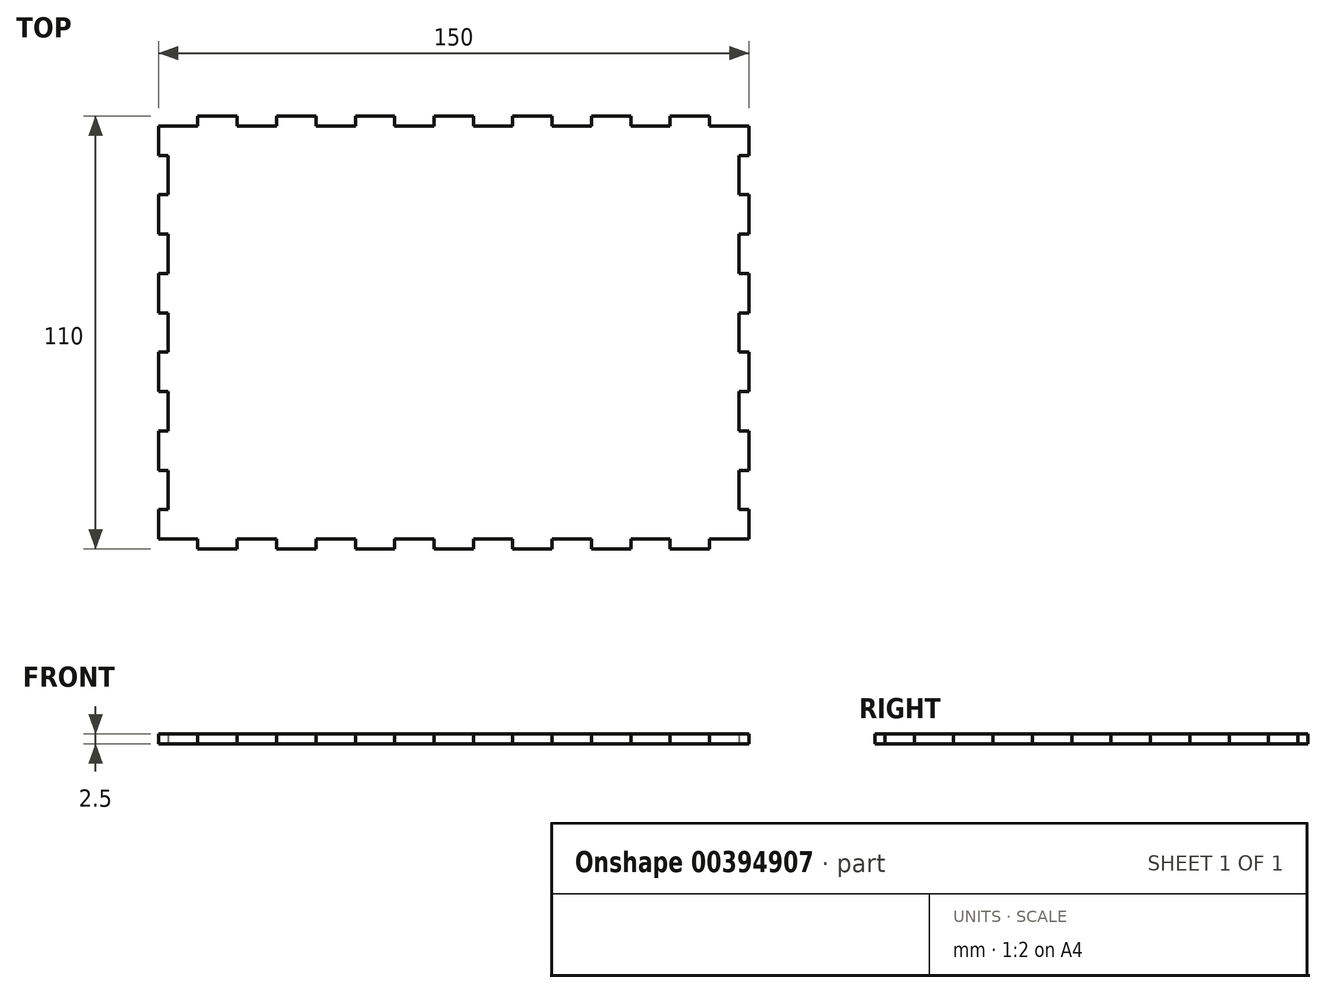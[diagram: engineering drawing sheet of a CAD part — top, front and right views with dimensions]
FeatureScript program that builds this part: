
annotation { "Feature Type Name" : "Feature", "Feature Type Description" : "" }
export const myFeature = defineFeature(function(context is Context, id is Id, definition is map)
    precondition{}
    {
        {
            var Q0;
            Q0=qCreatedBy(makeId("Top.planeOp"),FACE);
            var sketch = newSketch(context, id + "F0", { "sketchPlane" : qUnion([Q0])});
            skLineSegment(sketch, "E0.bottom", {"start": v(75, -55) * mm, "end": v(-75, -55) * mm});
            skLineSegment(sketch, "E0.top", {"start": v(75, 55) * mm, "end": v(-75, 55) * mm});
            skLineSegment(sketch, "E0.left", {"start": v(75, -55) * mm, "end": v(75, 55) * mm});
            skLineSegment(sketch, "E0.right", {"start": v(-75, -55) * mm, "end": v(-75, 55) * mm});
            skLineSegment(sketch, "E1.bottom", {"start": v(75, 55) * mm, "end": v(65, 55) * mm});
            skLineSegment(sketch, "E1.top", {"start": v(75, 52.5) * mm, "end": v(65, 52.5) * mm});
            skLineSegment(sketch, "E1.left", {"start": v(75, 55) * mm, "end": v(75, 52.5) * mm});
            skLineSegment(sketch, "E1.right", {"start": v(65, 55) * mm, "end": v(65, 52.5) * mm});
            skLineSegment(sketch, "E2.0.1.0", {"start": v(65, -52.5) * mm, "end": v(65, -55) * mm});
            skLineSegment(sketch, "E2.0.1.1", {"start": v(75, -52.5) * mm, "end": v(75, -55) * mm});
            skLineSegment(sketch, "E2.0.1.2", {"start": v(75, -55) * mm, "end": v(65, -55) * mm});
            skLineSegment(sketch, "E2.0.1.3", {"start": v(75, -52.5) * mm, "end": v(65, -52.5) * mm});
            skLineSegment(sketch, "E2.1.0.0", {"start": v(45, 55) * mm, "end": v(45, 52.5) * mm});
            skLineSegment(sketch, "E2.1.0.1", {"start": v(55, 55) * mm, "end": v(55, 52.5) * mm});
            skLineSegment(sketch, "E2.1.0.2", {"start": v(55, 52.5) * mm, "end": v(45, 52.5) * mm});
            skLineSegment(sketch, "E2.1.0.3", {"start": v(55, 55) * mm, "end": v(45, 55) * mm});
            skLineSegment(sketch, "E2.1.1.0", {"start": v(45, -52.5) * mm, "end": v(45, -55) * mm});
            skLineSegment(sketch, "E2.1.1.1", {"start": v(55, -52.5) * mm, "end": v(55, -55) * mm});
            skLineSegment(sketch, "E2.1.1.2", {"start": v(55, -55) * mm, "end": v(45, -55) * mm});
            skLineSegment(sketch, "E2.1.1.3", {"start": v(55, -52.5) * mm, "end": v(45, -52.5) * mm});
            skLineSegment(sketch, "E2.2.0.0", {"start": v(25, 55) * mm, "end": v(25, 52.5) * mm});
            skLineSegment(sketch, "E2.2.0.1", {"start": v(35, 55) * mm, "end": v(35, 52.5) * mm});
            skLineSegment(sketch, "E2.2.0.2", {"start": v(35, 52.5) * mm, "end": v(25, 52.5) * mm});
            skLineSegment(sketch, "E2.2.0.3", {"start": v(35, 55) * mm, "end": v(25, 55) * mm});
            skLineSegment(sketch, "E2.2.1.0", {"start": v(25, -52.5) * mm, "end": v(25, -55) * mm});
            skLineSegment(sketch, "E2.2.1.1", {"start": v(35, -52.5) * mm, "end": v(35, -55) * mm});
            skLineSegment(sketch, "E2.2.1.2", {"start": v(35, -55) * mm, "end": v(25, -55) * mm});
            skLineSegment(sketch, "E2.2.1.3", {"start": v(35, -52.5) * mm, "end": v(25, -52.5) * mm});
            skLineSegment(sketch, "E2.3.0.0", {"start": v(5, 55) * mm, "end": v(5, 52.5) * mm});
            skLineSegment(sketch, "E2.3.0.1", {"start": v(15, 55) * mm, "end": v(15, 52.5) * mm});
            skLineSegment(sketch, "E2.3.0.2", {"start": v(15, 52.5) * mm, "end": v(5, 52.5) * mm});
            skLineSegment(sketch, "E2.3.0.3", {"start": v(15, 55) * mm, "end": v(5, 55) * mm});
            skLineSegment(sketch, "E2.3.1.0", {"start": v(5, -52.5) * mm, "end": v(5, -55) * mm});
            skLineSegment(sketch, "E2.3.1.1", {"start": v(15, -52.5) * mm, "end": v(15, -55) * mm});
            skLineSegment(sketch, "E2.3.1.2", {"start": v(15, -55) * mm, "end": v(5, -55) * mm});
            skLineSegment(sketch, "E2.3.1.3", {"start": v(15, -52.5) * mm, "end": v(5, -52.5) * mm});
            skLineSegment(sketch, "E2.4.0.0", {"start": v(-15, 55) * mm, "end": v(-15, 52.5) * mm});
            skLineSegment(sketch, "E2.4.0.1", {"start": v(-5, 55) * mm, "end": v(-5, 52.5) * mm});
            skLineSegment(sketch, "E2.4.0.2", {"start": v(-5, 52.5) * mm, "end": v(-15, 52.5) * mm});
            skLineSegment(sketch, "E2.4.0.3", {"start": v(-5, 55) * mm, "end": v(-15, 55) * mm});
            skLineSegment(sketch, "E2.4.1.0", {"start": v(-15, -52.5) * mm, "end": v(-15, -55) * mm});
            skLineSegment(sketch, "E2.4.1.1", {"start": v(-5, -52.5) * mm, "end": v(-5, -55) * mm});
            skLineSegment(sketch, "E2.4.1.2", {"start": v(-5, -55) * mm, "end": v(-15, -55) * mm});
            skLineSegment(sketch, "E2.4.1.3", {"start": v(-5, -52.5) * mm, "end": v(-15, -52.5) * mm});
            skLineSegment(sketch, "E2.5.0.0", {"start": v(-35, 55) * mm, "end": v(-35, 52.5) * mm});
            skLineSegment(sketch, "E2.5.0.1", {"start": v(-25, 55) * mm, "end": v(-25, 52.5) * mm});
            skLineSegment(sketch, "E2.5.0.2", {"start": v(-25, 52.5) * mm, "end": v(-35, 52.5) * mm});
            skLineSegment(sketch, "E2.5.0.3", {"start": v(-25, 55) * mm, "end": v(-35, 55) * mm});
            skLineSegment(sketch, "E2.5.1.0", {"start": v(-35, -52.5) * mm, "end": v(-35, -55) * mm});
            skLineSegment(sketch, "E2.5.1.1", {"start": v(-25, -52.5) * mm, "end": v(-25, -55) * mm});
            skLineSegment(sketch, "E2.5.1.2", {"start": v(-25, -55) * mm, "end": v(-35, -55) * mm});
            skLineSegment(sketch, "E2.5.1.3", {"start": v(-25, -52.5) * mm, "end": v(-35, -52.5) * mm});
            skLineSegment(sketch, "E2.6.0.0", {"start": v(-55, 55) * mm, "end": v(-55, 52.5) * mm});
            skLineSegment(sketch, "E2.6.0.1", {"start": v(-45, 55) * mm, "end": v(-45, 52.5) * mm});
            skLineSegment(sketch, "E2.6.0.2", {"start": v(-45, 52.5) * mm, "end": v(-55, 52.5) * mm});
            skLineSegment(sketch, "E2.6.0.3", {"start": v(-45, 55) * mm, "end": v(-55, 55) * mm});
            skLineSegment(sketch, "E2.6.1.0", {"start": v(-55, -52.5) * mm, "end": v(-55, -55) * mm});
            skLineSegment(sketch, "E2.6.1.1", {"start": v(-45, -52.5) * mm, "end": v(-45, -55) * mm});
            skLineSegment(sketch, "E2.6.1.2", {"start": v(-45, -55) * mm, "end": v(-55, -55) * mm});
            skLineSegment(sketch, "E2.6.1.3", {"start": v(-45, -52.5) * mm, "end": v(-55, -52.5) * mm});
            skLineSegment(sketch, "E2.7.0.0", {"start": v(-75, 55) * mm, "end": v(-75, 52.5) * mm});
            skLineSegment(sketch, "E2.7.0.1", {"start": v(-65, 55) * mm, "end": v(-65, 52.5) * mm});
            skLineSegment(sketch, "E2.7.0.2", {"start": v(-65, 52.5) * mm, "end": v(-75, 52.5) * mm});
            skLineSegment(sketch, "E2.7.0.3", {"start": v(-65, 55) * mm, "end": v(-75, 55) * mm});
            skLineSegment(sketch, "E2.7.1.0", {"start": v(-75, -52.5) * mm, "end": v(-75, -55) * mm});
            skLineSegment(sketch, "E2.7.1.1", {"start": v(-65, -52.5) * mm, "end": v(-65, -55) * mm});
            skLineSegment(sketch, "E2.7.1.2", {"start": v(-65, -55) * mm, "end": v(-75, -55) * mm});
            skLineSegment(sketch, "E2.7.1.3", {"start": v(-65, -52.5) * mm, "end": v(-75, -52.5) * mm});
            skLineSegment(sketch, "E2.direction1", {"start": v(65, 52.5) * mm, "end": v(45, 52.5) * mm, "construction": true});
            skLineSegment(sketch, "E2.direction2", {"start": v(65, 52.5) * mm, "end": v(65, -55) * mm, "construction": true});
            skLineSegment(sketch, "E3", {"start": v(-75, 52.5) * mm, "end": v(-75, 45) * mm, "construction": true});
            skLineSegment(sketch, "E4.bottom", {"start": v(-75, 45) * mm, "end": v(-72.5, 45) * mm});
            skLineSegment(sketch, "E4.top", {"start": v(-75, 35) * mm, "end": v(-72.5, 35) * mm});
            skLineSegment(sketch, "E4.left", {"start": v(-75, 45) * mm, "end": v(-75, 35) * mm});
            skLineSegment(sketch, "E4.right", {"start": v(-72.5, 45) * mm, "end": v(-72.5, 35) * mm});
            skLineSegment(sketch, "E5.0.1.0", {"start": v(-72.5, 25) * mm, "end": v(-72.5, 15) * mm});
            skLineSegment(sketch, "E5.0.1.1", {"start": v(-75, 25) * mm, "end": v(-75, 15) * mm});
            skLineSegment(sketch, "E5.0.1.2", {"start": v(-75, 25) * mm, "end": v(-72.5, 25) * mm});
            skLineSegment(sketch, "E5.0.1.3", {"start": v(-75, 15) * mm, "end": v(-72.5, 15) * mm});
            skLineSegment(sketch, "E5.0.2.0", {"start": v(-72.5, 5) * mm, "end": v(-72.5, -5) * mm});
            skLineSegment(sketch, "E5.0.2.1", {"start": v(-75, 5) * mm, "end": v(-75, -5) * mm});
            skLineSegment(sketch, "E5.0.2.2", {"start": v(-75, 5) * mm, "end": v(-72.5, 5) * mm});
            skLineSegment(sketch, "E5.0.2.3", {"start": v(-75, -5) * mm, "end": v(-72.5, -5) * mm});
            skLineSegment(sketch, "E5.0.3.0", {"start": v(-72.5, -15) * mm, "end": v(-72.5, -25) * mm});
            skLineSegment(sketch, "E5.0.3.1", {"start": v(-75, -15) * mm, "end": v(-75, -25) * mm});
            skLineSegment(sketch, "E5.0.3.2", {"start": v(-75, -15) * mm, "end": v(-72.5, -15) * mm});
            skLineSegment(sketch, "E5.0.3.3", {"start": v(-75, -25) * mm, "end": v(-72.5, -25) * mm});
            skLineSegment(sketch, "E5.0.4.0", {"start": v(-72.5, -35) * mm, "end": v(-72.5, -45) * mm});
            skLineSegment(sketch, "E5.0.4.1", {"start": v(-75, -35) * mm, "end": v(-75, -45) * mm});
            skLineSegment(sketch, "E5.0.4.2", {"start": v(-75, -35) * mm, "end": v(-72.5, -35) * mm});
            skLineSegment(sketch, "E5.0.4.3", {"start": v(-75, -45) * mm, "end": v(-72.5, -45) * mm});
            skLineSegment(sketch, "E5.1.0.0", {"start": v(75, 45) * mm, "end": v(75, 35) * mm});
            skLineSegment(sketch, "E5.1.0.1", {"start": v(72.5, 45) * mm, "end": v(72.5, 35) * mm});
            skLineSegment(sketch, "E5.1.0.2", {"start": v(72.5, 45) * mm, "end": v(75, 45) * mm});
            skLineSegment(sketch, "E5.1.0.3", {"start": v(72.5, 35) * mm, "end": v(75, 35) * mm});
            skLineSegment(sketch, "E5.1.1.0", {"start": v(75, 25) * mm, "end": v(75, 15) * mm});
            skLineSegment(sketch, "E5.1.1.1", {"start": v(72.5, 25) * mm, "end": v(72.5, 15) * mm});
            skLineSegment(sketch, "E5.1.1.2", {"start": v(72.5, 25) * mm, "end": v(75, 25) * mm});
            skLineSegment(sketch, "E5.1.1.3", {"start": v(72.5, 15) * mm, "end": v(75, 15) * mm});
            skLineSegment(sketch, "E5.1.2.0", {"start": v(75, 5) * mm, "end": v(75, -5) * mm});
            skLineSegment(sketch, "E5.1.2.1", {"start": v(72.5, 5) * mm, "end": v(72.5, -5) * mm});
            skLineSegment(sketch, "E5.1.2.2", {"start": v(72.5, 5) * mm, "end": v(75, 5) * mm});
            skLineSegment(sketch, "E5.1.2.3", {"start": v(72.5, -5) * mm, "end": v(75, -5) * mm});
            skLineSegment(sketch, "E5.1.3.0", {"start": v(75, -15) * mm, "end": v(75, -25) * mm});
            skLineSegment(sketch, "E5.1.3.1", {"start": v(72.5, -15) * mm, "end": v(72.5, -25) * mm});
            skLineSegment(sketch, "E5.1.3.2", {"start": v(72.5, -15) * mm, "end": v(75, -15) * mm});
            skLineSegment(sketch, "E5.1.3.3", {"start": v(72.5, -25) * mm, "end": v(75, -25) * mm});
            skLineSegment(sketch, "E5.1.4.0", {"start": v(75, -35) * mm, "end": v(75, -45) * mm});
            skLineSegment(sketch, "E5.1.4.1", {"start": v(72.5, -35) * mm, "end": v(72.5, -45) * mm});
            skLineSegment(sketch, "E5.1.4.2", {"start": v(72.5, -35) * mm, "end": v(75, -35) * mm});
            skLineSegment(sketch, "E5.1.4.3", {"start": v(72.5, -45) * mm, "end": v(75, -45) * mm});
            skLineSegment(sketch, "E5.direction1", {"start": v(-72.5, 35) * mm, "end": v(75, 35) * mm, "construction": true});
            skLineSegment(sketch, "E5.direction2", {"start": v(-72.5, 35) * mm, "end": v(-72.5, 15) * mm, "construction": true});
            skSolve(sketch);
        }
        {
            var Q0;
            Q0=makeQuery(id+"F0.imprint","IMPRINT",FACE,{"disambiguationData":[TD([[makeQuery(id+"F0.imprint","IMPRINT",EDGE,{"derivedFrom":sQuery(id+"F0.wireOp",EDGE,"E0.bottom")}),-1.0]])]});
            extrude(context, id + "F1", {"entities" : qUnion([Q0]), "depth" : 2.5 * mm});
        }
    });
